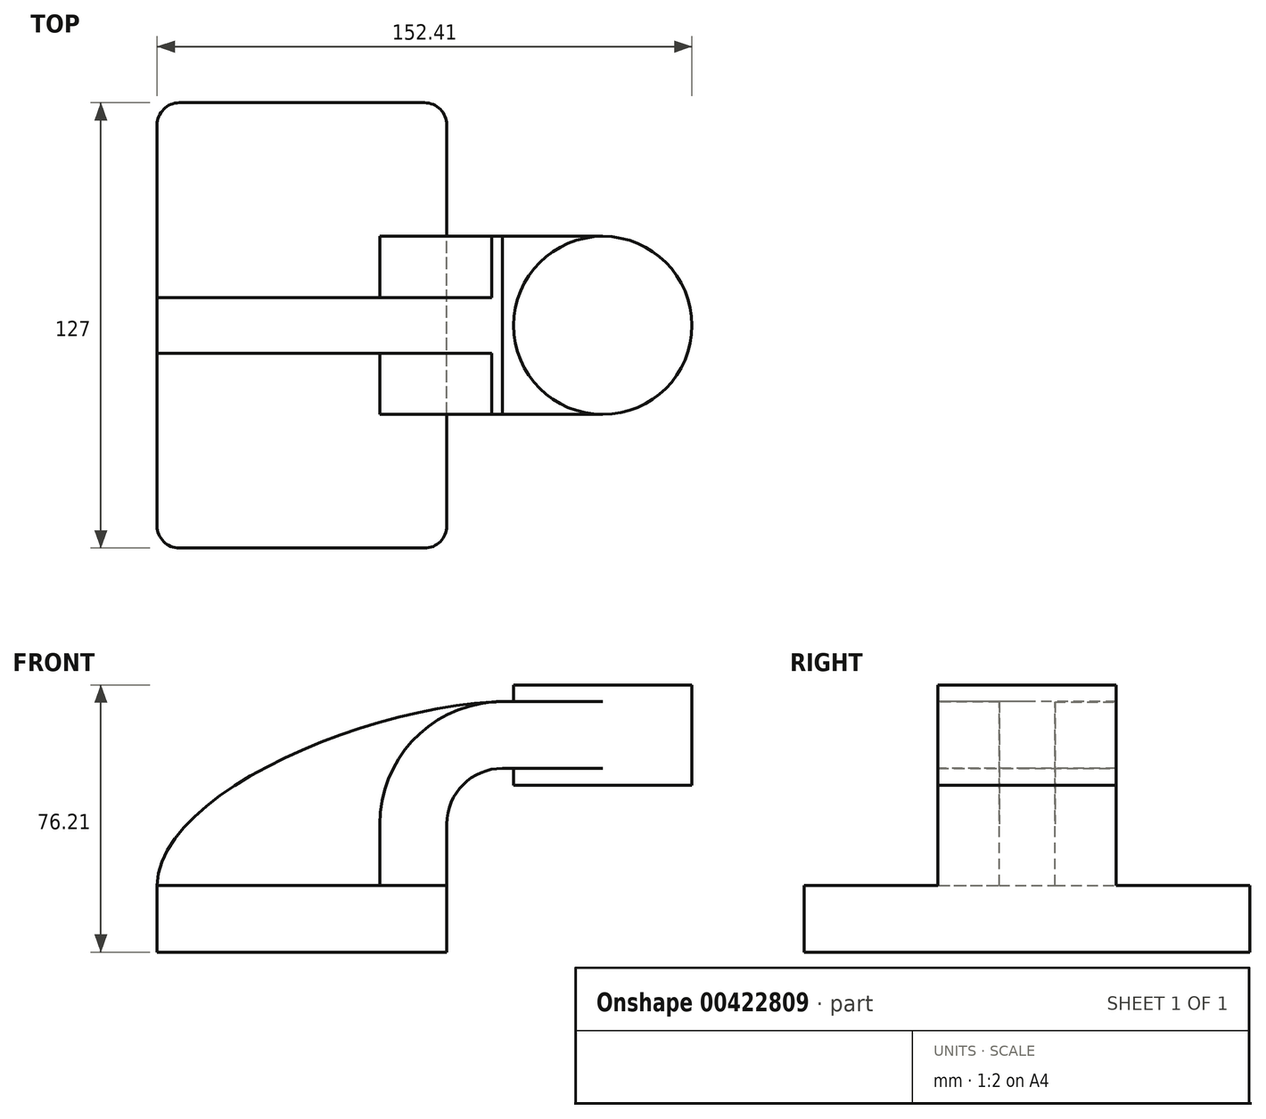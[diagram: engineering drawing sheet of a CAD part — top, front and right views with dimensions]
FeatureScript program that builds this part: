
annotation { "Feature Type Name" : "Feature", "Feature Type Description" : "" }
export const myFeature = defineFeature(function(context is Context, id is Id, definition is map)
    precondition{}
    {
        {
            var Q0;
            Q0=qCreatedBy(makeId("Front.planeOp"),FACE);
            var sketch = newSketch(context, id + "F0", { "sketchPlane" : qUnion([Q0])});
            skLineSegment(sketch, "E0.bottom", {"start": v(-41.27, -9.53) * mm, "end": v(41.28, -9.53) * mm});
            skLineSegment(sketch, "E0.top", {"start": v(-41.28, 9.53) * mm, "end": v(41.28, 9.53) * mm});
            skLineSegment(sketch, "E0.left", {"start": v(-41.28, -9.53) * mm, "end": v(-41.28, 9.53) * mm});
            skLineSegment(sketch, "E0.right", {"start": v(41.28, -9.53) * mm, "end": v(41.28, 9.52) * mm});
            skPoint(sketch, "E0.middle", {"position": v(0, 0) * mm});
            skLineSegment(sketch, "E1.bottom", {"start": v(60.32, 38.1) * mm, "end": v(111.12, 38.1) * mm});
            skLineSegment(sketch, "E1.top", {"start": v(60.32, 66.67) * mm, "end": v(111.12, 66.67) * mm});
            skLineSegment(sketch, "E1.left", {"start": v(60.32, 38.1) * mm, "end": v(60.32, 66.67) * mm});
            skLineSegment(sketch, "E1.right", {"start": v(111.12, 38.1) * mm, "end": v(111.12, 66.67) * mm});
            skPoint(sketch, "E1.middle", {"position": v(85.72, 52.39) * mm});
            skLineSegment(sketch, "E2", {"start": v(41.28, 9.52) * mm, "end": v(41.28, 27) * mm});
            skArc(sketch, "E3", {"start": v(41.27, 27) * mm, "mid": v(45.92, 38.23) * mm, "end": v(57.15, 42.88) * mm});
            skLineSegment(sketch, "E4", {"start": v(57.15, 42.88) * mm, "end": v(85.72, 42.88) * mm});
            skLineSegment(sketch, "E5.0", {"start": v(57.15, 61.93) * mm, "end": v(85.72, 61.93) * mm});
            skArc(sketch, "E5.1", {"start": v(22.22, 27) * mm, "mid": v(32.45, 51.7) * mm, "end": v(57.15, 61.93) * mm});
            skLineSegment(sketch, "E5.2", {"start": v(22.22, 9.52) * mm, "end": v(22.22, 27) * mm});
            skLineSegment(sketch, "E6", {"start": v(85.72, 38.1) * mm, "end": v(85.72, 66.67) * mm});
            skFitSpline(sketch, "E7", {"points": [v(-41.28, 9.53) * mm, v(57.15, 61.93) * mm], "startDerivative": vector(1.58, 79.95) * mm, "endDerivative": vector(112.62, 3.14) * mm});
            skSolve(sketch);
        }
        {
            var Q0;
            Q0=makeQuery(id+"F0.imprint","IMPRINT",FACE,{"disambiguationData":[TD([[makeQuery(id+"F0.imprint","IMPRINT",EDGE,{"derivedFrom":sQuery(id+"F0.wireOp",EDGE,"E0.bottom")}),1.0]])]});
            extrude(context, id + "F1", {"entities" : qUnion([Q0]), "endBound" : BoundingType.SYMMETRIC, "depth" : 127 * mm});
        }
        {
            var Q0;
            {var subQ0=sQuery(id+"F0.wireOp",EDGE,"E4");var subQ1=sQuery(id+"F0.wireOp",EDGE,"E1.left");var subQ2=makeQuery(id+"F0.imprint","INTERSECT",VERTEX,{"derivedFrom":[subQ1,subQ0]});Q0=makeQuery(id+"F0.imprint","IMPRINT",FACE,{"disambiguationData":[TD([[makeQuery(id+"F0.imprint","IMPRINT",EDGE,{"disambiguationData":[TD([[subQ2,-1.0]])],"derivedFrom":subQ1}),-1.0]])]});}
            var Q1;
            {var subQ1=sQuery(id+"F0.wireOp",EDGE,"E2");Q1=makeQuery(id+"F0.imprint","IMPRINT",FACE,{"disambiguationData":[TD([[makeQuery(id+"F0.imprint","IMPRINT",EDGE,{"derivedFrom":subQ1}),1.0]])]});}
            extrude(context, id + "F2", {"entities" : qUnion([Q0, Q1]), "operationType" : NewBodyOperationType.ADD, "endBound" : BoundingType.SYMMETRIC, "depth" : 50.8 * mm});
        }
        {
            var Q0;
            {var subQ3=sQuery(id+"F0.wireOp",EDGE,"E5.2");Q0=makeQuery(id+"F0.imprint","IMPRINT",FACE,{"disambiguationData":[TD([[makeQuery(id+"F0.imprint","IMPRINT",EDGE,{"derivedFrom":subQ3}),1.0]])]});}
            extrude(context, id + "F3", {"entities" : qUnion([Q0]), "operationType" : NewBodyOperationType.ADD, "endBound" : BoundingType.SYMMETRIC, "depth" : 15.88 * mm});
        }
        {
            var Q0;
            {var subQ4=sQuery(id+"F0.wireOp",EDGE,"E1.right");Q0=makeQuery(id+"F0.imprint","IMPRINT",FACE,{"disambiguationData":[TD([[makeQuery(id+"F0.imprint","IMPRINT",EDGE,{"derivedFrom":subQ4}),1.0]])]});}
            var Q1;
            Q1=sQuery(id+"F0.wireOp",EDGE,"E6");
            revolve(context, id + "F4", {"operationType" : NewBodyOperationType.ADD, "entities" : qUnion([Q0]), "axis" : qUnion([Q1]), "revolveType" : RevolveType.FULL});
        }
        {
            var Q0;
            Q0=makeQuery(id+"F1.opExtrude","CAP_EDGE",EDGE,{"disambiguationData":[OSD([sQuery(id+"F0.wireOp",EDGE,"E0.right")])],"isStart":false});
            var Q1;
            Q1=makeQuery(id+"F1.opExtrude","CAP_EDGE",EDGE,{"disambiguationData":[OSD([sQuery(id+"F0.wireOp",EDGE,"E0.left")])],"isStart":false});
            var Q2;
            Q2=makeQuery(id+"F1.opExtrude","CAP_EDGE",EDGE,{"disambiguationData":[OSD([sQuery(id+"F0.wireOp",EDGE,"E0.right")])],"isStart":true});
            var Q3;
            Q3=makeQuery(id+"F1.opExtrude","CAP_EDGE",EDGE,{"disambiguationData":[OSD([sQuery(id+"F0.wireOp",EDGE,"E0.left")])],"isStart":true});
            fillet(context, id + "F5", {"entities" : qUnion([Q0, Q1, Q2, Q3]), "radius" : 6.35 * mm, "tangentPropagation" : true, "allowEdgeOverflow" : false});
        }
    });
